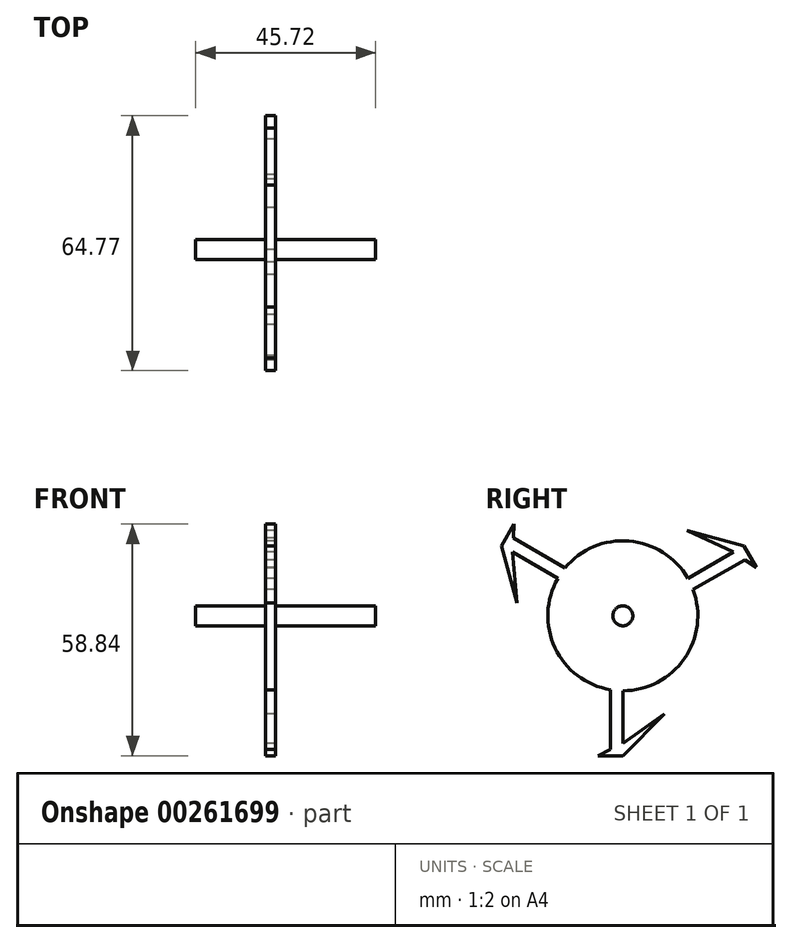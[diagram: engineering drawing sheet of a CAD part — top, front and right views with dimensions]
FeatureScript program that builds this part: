
annotation { "Feature Type Name" : "Feature", "Feature Type Description" : "" }
export const myFeature = defineFeature(function(context is Context, id is Id, definition is map)
    precondition{}
    {
        {
            var Q0;
            Q0=qCreatedBy(makeId("Right.planeOp"),FACE);
            var sketch = newSketch(context, id + "F0", { "sketchPlane" : qUnion([Q0])});
            skCircle(sketch, "E0", {"center": v(0, 0) * mm, "radius": 19.05 * mm});
            skLineSegment(sketch, "E1", {"start": v(32.38, 15.03) * mm, "end": v(1.59, -2.75) * mm});
            skCircle(sketch, "E2", {"center": v(0, 0) * mm, "radius": 2.54 * mm});
            skLineSegment(sketch, "E3", {"start": v(30.8, 17.78) * mm, "end": v(33.97, 12.28) * mm});
            skLineSegment(sketch, "E4", {"start": v(33.97, 12.28) * mm, "end": v(28.05, 16.2) * mm});
            skLineSegment(sketch, "E5", {"start": v(0, 0) * mm, "end": v(30.8, 17.78) * mm});
            skLineSegment(sketch, "E6", {"start": v(0, 0) * mm, "end": v(0, -35.56) * mm});
            skLineSegment(sketch, "E7", {"start": v(0, 0) * mm, "end": v(-30.8, 17.78) * mm});
            skLineSegment(sketch, "E8", {"start": v(-3.18, 0) * mm, "end": v(-3.18, -35.56) * mm});
            skLineSegment(sketch, "E9", {"start": v(0, -35.56) * mm, "end": v(-6.35, -35.56) * mm});
            skLineSegment(sketch, "E10", {"start": v(-6.35, -35.56) * mm, "end": v(0, -32.39) * mm});
            skLineSegment(sketch, "E11", {"start": v(1.59, 2.75) * mm, "end": v(-29.2, 20.53) * mm});
            skLineSegment(sketch, "E12", {"start": v(-30.8, 17.78) * mm, "end": v(-27.62, 23.28) * mm});
            skLineSegment(sketch, "E13", {"start": v(-27.62, 23.28) * mm, "end": v(-28.05, 16.2) * mm});
            skLineSegment(sketch, "E14", {"start": v(-3.18, 0) * mm, "end": v(0, 0) * mm});
            skLineSegment(sketch, "E15", {"start": v(0, 0) * mm, "end": v(1.59, 2.75) * mm});
            skLineSegment(sketch, "E16", {"start": v(0, -35.56) * mm, "end": v(10.6, -24.97) * mm});
            skLineSegment(sketch, "E17", {"start": v(10.6, -24.97) * mm, "end": v(0, -32.39) * mm});
            skLineSegment(sketch, "E18", {"start": v(-30.8, 17.78) * mm, "end": v(-26.92, 3.31) * mm});
            skLineSegment(sketch, "E19", {"start": v(-26.92, 3.31) * mm, "end": v(-28.05, 16.2) * mm});
            skLineSegment(sketch, "E20", {"start": v(30.8, 17.78) * mm, "end": v(16.33, 21.66) * mm});
            skLineSegment(sketch, "E21", {"start": v(16.33, 21.66) * mm, "end": v(28.05, 16.2) * mm});
            skLineSegment(sketch, "E22", {"start": v(1.59, -2.75) * mm, "end": v(0, 0) * mm});
            skSolve(sketch);
        }
        {
            var Q0;
            Q0 = qSketchRegion(id + "F0", true);
            extrude(context, id + "F1", {"entities" : qUnion([Q0]), "depth" : 2.54 * mm});
        }
        {
            var Q0;
            {var subQ0=sQuery(id+"F0.wireOp",EDGE,"E15");var subQ1=sQuery(id+"F0.wireOp",EDGE,"E2");var subQ2=makeQuery(id+"F0.imprint","INTERSECT",VERTEX,{"derivedFrom":[subQ1,subQ0]});Q0=makeQuery(id+"F0.imprint","IMPRINT",FACE,{"disambiguationData":[TD([[makeQuery(id+"F0.imprint","IMPRINT",EDGE,{"disambiguationData":[TD([[subQ2,-1.0]])],"derivedFrom":subQ1}),1.0]])]});}
            var Q1;
            {var subQ0=sQuery(id+"F0.wireOp",EDGE,"E7");var subQ1=sQuery(id+"F0.wireOp",EDGE,"E2");var subQ2=makeQuery(id+"F0.imprint","INTERSECT",VERTEX,{"derivedFrom":[subQ1,subQ0]});Q1=makeQuery(id+"F0.imprint","IMPRINT",FACE,{"disambiguationData":[TD([[makeQuery(id+"F0.imprint","IMPRINT",EDGE,{"disambiguationData":[TD([[subQ2,-1.0]])],"derivedFrom":subQ1}),1.0]])]});}
            var Q2;
            {var subQ0=sQuery(id+"F0.wireOp",EDGE,"E14");var subQ1=sQuery(id+"F0.wireOp",EDGE,"E2");var subQ2=makeQuery(id+"F0.imprint","INTERSECT",VERTEX,{"derivedFrom":[subQ1,subQ0]});Q2=makeQuery(id+"F0.imprint","IMPRINT",FACE,{"disambiguationData":[TD([[makeQuery(id+"F0.imprint","IMPRINT",EDGE,{"disambiguationData":[TD([[subQ2,-1.0]])],"derivedFrom":subQ1}),1.0]])]});}
            var Q3;
            {var subQ0=sQuery(id+"F0.wireOp",EDGE,"E6");var subQ1=sQuery(id+"F0.wireOp",EDGE,"E2");var subQ2=makeQuery(id+"F0.imprint","INTERSECT",VERTEX,{"derivedFrom":[subQ1,subQ0]});Q3=makeQuery(id+"F0.imprint","IMPRINT",FACE,{"disambiguationData":[TD([[makeQuery(id+"F0.imprint","IMPRINT",EDGE,{"disambiguationData":[TD([[subQ2,-1.0]])],"derivedFrom":subQ1}),1.0]])]});}
            var Q4;
            {var subQ0=sQuery(id+"F0.wireOp",EDGE,"E5");var subQ1=sQuery(id+"F0.wireOp",EDGE,"E2");var subQ2=makeQuery(id+"F0.imprint","INTERSECT",VERTEX,{"derivedFrom":[subQ1,subQ0]});Q4=makeQuery(id+"F0.imprint","IMPRINT",FACE,{"disambiguationData":[TD([[makeQuery(id+"F0.imprint","IMPRINT",EDGE,{"disambiguationData":[TD([[subQ2,1.0]])],"derivedFrom":subQ1}),1.0]])]});}
            var Q5;
            {var subQ0=sQuery(id+"F0.wireOp",EDGE,"E15");var subQ1=sQuery(id+"F0.wireOp",EDGE,"E2");var subQ2=makeQuery(id+"F0.imprint","INTERSECT",VERTEX,{"derivedFrom":[subQ1,subQ0]});Q5=makeQuery(id+"F0.imprint","IMPRINT",FACE,{"disambiguationData":[TD([[makeQuery(id+"F0.imprint","IMPRINT",EDGE,{"disambiguationData":[TD([[subQ2,1.0]])],"derivedFrom":subQ1}),1.0]])]});}
            extrude(context, id + "F2", {"entities" : qUnion([Q0, Q1, Q2, Q3, Q4, Q5]), "operationType" : NewBodyOperationType.ADD, "depth" : 27.94 * mm});
        }
        {
            var Q0;
            {var subQ0=sQuery(id+"F0.wireOp",EDGE,"E5");var subQ1=sQuery(id+"F0.wireOp",EDGE,"E2");var subQ2=makeQuery(id+"F0.imprint","INTERSECT",VERTEX,{"derivedFrom":[subQ1,subQ0]});Q0=makeQuery(id+"F0.imprint","IMPRINT",FACE,{"disambiguationData":[TD([[makeQuery(id+"F0.imprint","IMPRINT",EDGE,{"disambiguationData":[TD([[subQ2,1.0]])],"derivedFrom":subQ1}),1.0]])]});}
            var Q1;
            {var subQ0=sQuery(id+"F0.wireOp",EDGE,"E6");var subQ1=sQuery(id+"F0.wireOp",EDGE,"E2");var subQ2=makeQuery(id+"F0.imprint","INTERSECT",VERTEX,{"derivedFrom":[subQ1,subQ0]});Q1=makeQuery(id+"F0.imprint","IMPRINT",FACE,{"disambiguationData":[TD([[makeQuery(id+"F0.imprint","IMPRINT",EDGE,{"disambiguationData":[TD([[subQ2,-1.0]])],"derivedFrom":subQ1}),1.0]])]});}
            var Q2;
            {var subQ0=sQuery(id+"F0.wireOp",EDGE,"E14");var subQ1=sQuery(id+"F0.wireOp",EDGE,"E2");var subQ2=makeQuery(id+"F0.imprint","INTERSECT",VERTEX,{"derivedFrom":[subQ1,subQ0]});Q2=makeQuery(id+"F0.imprint","IMPRINT",FACE,{"disambiguationData":[TD([[makeQuery(id+"F0.imprint","IMPRINT",EDGE,{"disambiguationData":[TD([[subQ2,-1.0]])],"derivedFrom":subQ1}),1.0]])]});}
            var Q3;
            {var subQ0=sQuery(id+"F0.wireOp",EDGE,"E7");var subQ1=sQuery(id+"F0.wireOp",EDGE,"E2");var subQ2=makeQuery(id+"F0.imprint","INTERSECT",VERTEX,{"derivedFrom":[subQ1,subQ0]});Q3=makeQuery(id+"F0.imprint","IMPRINT",FACE,{"disambiguationData":[TD([[makeQuery(id+"F0.imprint","IMPRINT",EDGE,{"disambiguationData":[TD([[subQ2,-1.0]])],"derivedFrom":subQ1}),1.0]])]});}
            var Q4;
            {var subQ0=sQuery(id+"F0.wireOp",EDGE,"E15");var subQ1=sQuery(id+"F0.wireOp",EDGE,"E2");var subQ2=makeQuery(id+"F0.imprint","INTERSECT",VERTEX,{"derivedFrom":[subQ1,subQ0]});Q4=makeQuery(id+"F0.imprint","IMPRINT",FACE,{"disambiguationData":[TD([[makeQuery(id+"F0.imprint","IMPRINT",EDGE,{"disambiguationData":[TD([[subQ2,-1.0]])],"derivedFrom":subQ1}),1.0]])]});}
            var Q5;
            {var subQ0=sQuery(id+"F0.wireOp",EDGE,"E15");var subQ1=sQuery(id+"F0.wireOp",EDGE,"E2");var subQ2=makeQuery(id+"F0.imprint","INTERSECT",VERTEX,{"derivedFrom":[subQ1,subQ0]});Q5=makeQuery(id+"F0.imprint","IMPRINT",FACE,{"disambiguationData":[TD([[makeQuery(id+"F0.imprint","IMPRINT",EDGE,{"disambiguationData":[TD([[subQ2,1.0]])],"derivedFrom":subQ1}),1.0]])]});}
            extrude(context, id + "F3", {"entities" : qUnion([Q0, Q1, Q2, Q3, Q4, Q5]), "operationType" : NewBodyOperationType.ADD, "oppositeDirection" : true, "depth" : 17.78 * mm});
        }
    });
